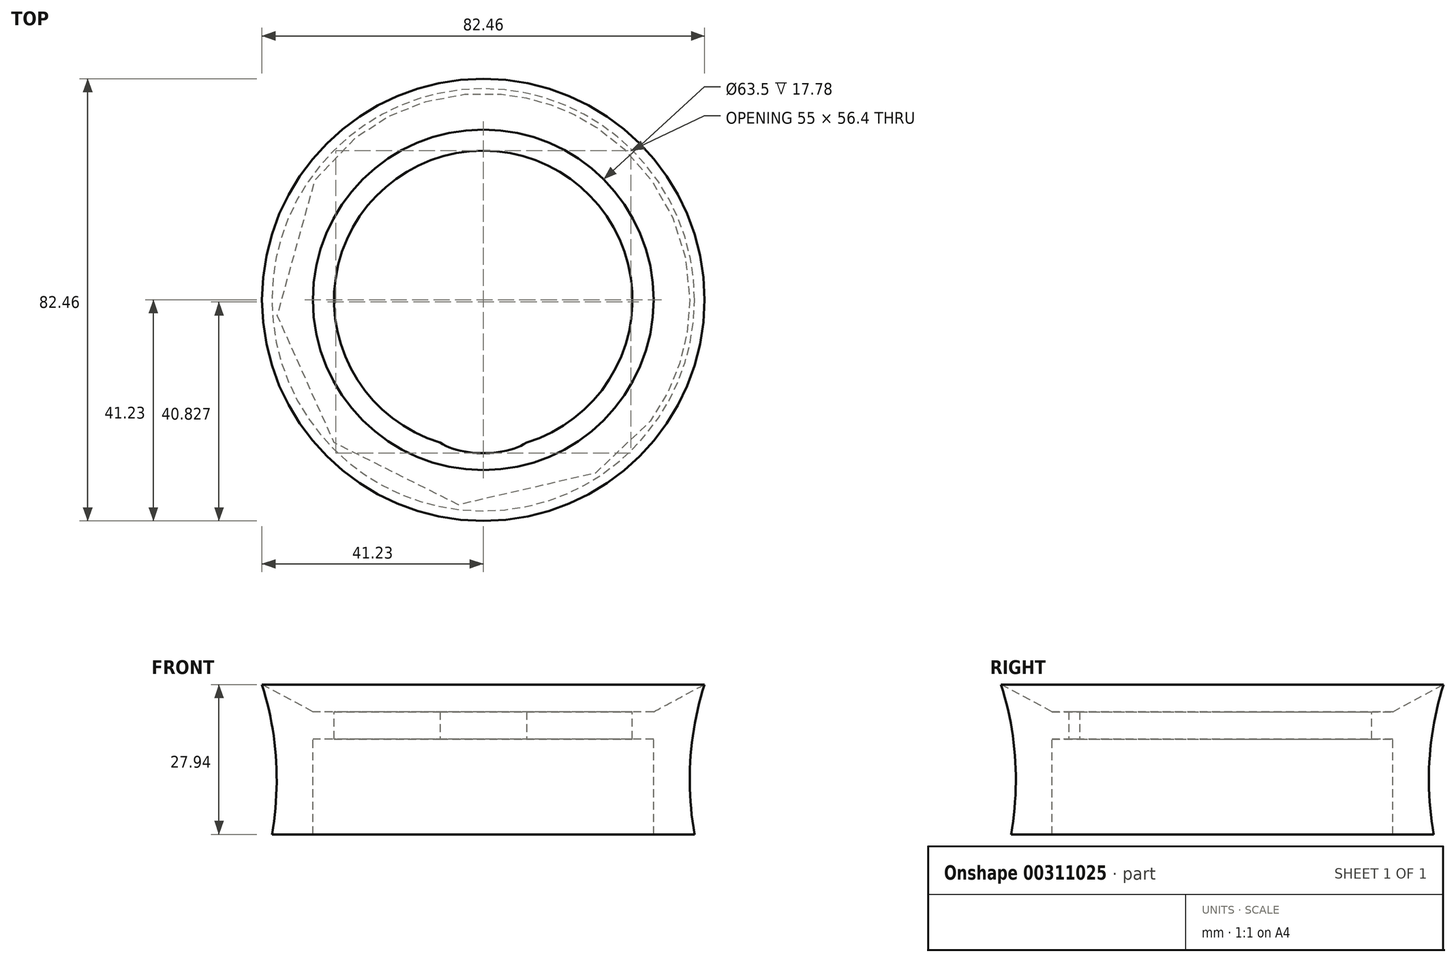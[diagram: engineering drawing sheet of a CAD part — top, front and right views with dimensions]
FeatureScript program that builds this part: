
annotation { "Feature Type Name" : "Feature", "Feature Type Description" : "" }
export const myFeature = defineFeature(function(context is Context, id is Id, definition is map)
    precondition{}
    {
        {
            var Q0;
            Q0=qCreatedBy(makeId("Front.planeOp"),FACE);
            var sketch = newSketch(context, id + "F0", { "sketchPlane" : qUnion([Q0])});
            skLineSegment(sketch, "E0", {"start": v(-41.23, 17.38) * mm, "end": v(0, 17.38) * mm});
            skLineSegment(sketch, "E1", {"start": v(0, 17.38) * mm, "end": v(0, -10.56) * mm});
            skLineSegment(sketch, "E2", {"start": v(0, -10.56) * mm, "end": v(-39.37, -10.56) * mm});
            skArc(sketch, "E3", {"start": v(-39.37, -10.56) * mm, "mid": v(-38.62, 3.52) * mm, "end": v(-41.23, 17.38) * mm});
            skLineSegment(sketch, "E4", {"start": v(-31.75, -10.56) * mm, "end": v(-31.75, 7.22) * mm});
            skLineSegment(sketch, "E5", {"start": v(0, 7.22) * mm, "end": v(0, 12.3) * mm});
            skLineSegment(sketch, "E6", {"start": v(-31.75, 12.3) * mm, "end": v(-41.23, 17.38) * mm});
            skLineSegment(sketch, "E7", {"start": v(-31.75, 7.22) * mm, "end": v(0, 7.22) * mm});
            skLineSegment(sketch, "E8", {"start": v(0, 12.3) * mm, "end": v(-31.75, 12.3) * mm});
            skLineSegment(sketch, "E9", {"start": v(-27.8, 7.22) * mm, "end": v(-18.9, 7.22) * mm});
            skLineSegment(sketch, "E10", {"start": v(-18.9, 7.22) * mm, "end": v(-18.9, 12.3) * mm});
            skLineSegment(sketch, "E11", {"start": v(-18.9, 12.3) * mm, "end": v(-27.8, 12.3) * mm});
            skLineSegment(sketch, "E12", {"start": v(-27.8, 12.3) * mm, "end": v(-27.8, 7.22) * mm});
            skSolve(sketch);
        }
        {
            var Q0;
            Q0=qCreatedBy(makeId("Top.planeOp"),FACE);
            var sketch = newSketch(context, id + "F1", { "sketchPlane" : qUnion([Q0])});
            skEllipse(sketch, "E13", {"center": v(0, -23.5) * mm, "majorRadius": 10.16 * mm, "minorRadius": 5.1 * mm, "majorAxis": v(-1, 0)});
            skSolve(sketch);
        }
        {
            var Q0;
            {var subQ2=sQuery(id+"F0.wireOp",EDGE,"E3");Q0=makeQuery(id+"F0.imprint","IMPRINT",FACE,{"disambiguationData":[TD([[makeQuery(id+"F0.imprint","IMPRINT",EDGE,{"derivedFrom":subQ2}),-1.0]])]});}
            var Q1;
            Q1=makeQuery(id+"F0.imprint","IMPRINT",FACE,{"disambiguationData":[TD([[makeQuery(id+"F0.imprint","IMPRINT",EDGE,{"derivedFrom":sQuery(id+"F0.wireOp",EDGE,"E9")}),1.0]])]});
            var Q2;
            {var subQ0=sQuery(id+"F0.wireOp",EDGE,"E5");Q2=makeQuery(id+"F0.imprint","IMPRINT",FACE,{"disambiguationData":[TD([[makeQuery(id+"F0.imprint","IMPRINT",EDGE,{"derivedFrom":subQ0}),1.0]])]});}
            var Q3;
            Q3=sQuery(id+"F0.wireOp",EDGE,"E1");
            revolve(context, id + "F2", {"entities" : qUnion([Q0, Q1, Q2]), "axis" : qUnion([Q3]), "revolveType" : RevolveType.FULL});
        }
        {
            var Q0;
            Q0 = qSketchRegion(id + "F1", true);
            extrude(context, id + "F3", {"entities" : qUnion([Q0]), "operationType" : NewBodyOperationType.REMOVE, "depth" : 27.94 * mm});
        }
    });
